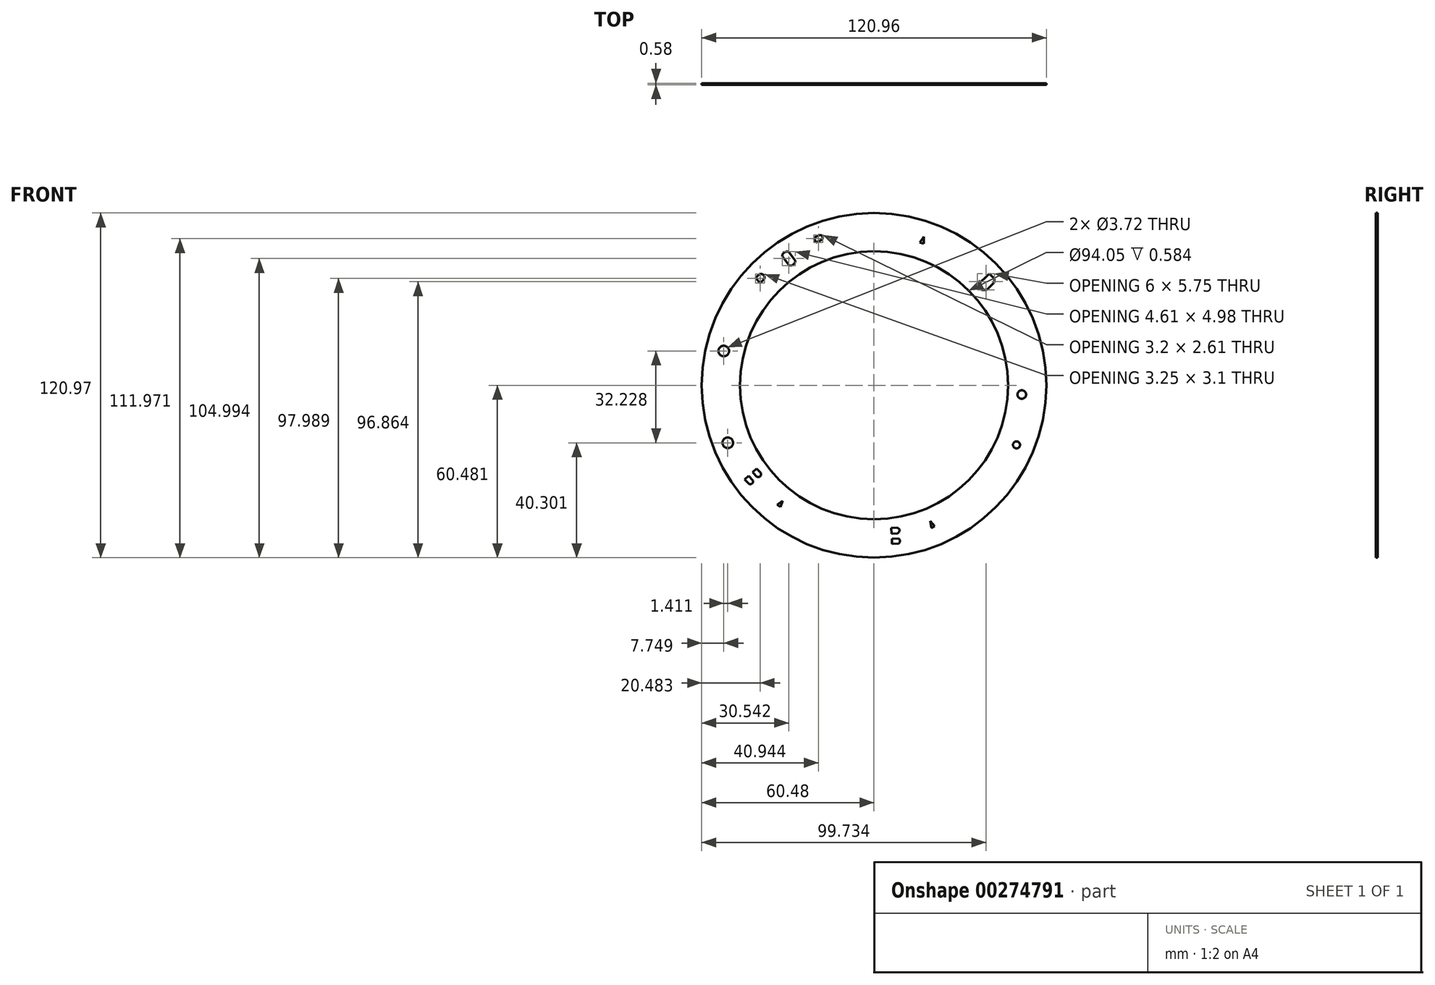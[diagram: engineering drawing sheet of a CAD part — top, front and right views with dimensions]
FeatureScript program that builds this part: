
annotation { "Feature Type Name" : "Feature", "Feature Type Description" : "" }
export const myFeature = defineFeature(function(context is Context, id is Id, definition is map)
    precondition{}
    {
        {
            var Q0;
            Q0=qCreatedBy(makeId("Front.planeOp"),FACE);
            var sketch = newSketch(context, id + "F0", { "sketchPlane" : qUnion([Q0])});
            skLineSegment(sketch, "E0", {"start": v(-42.5, 39.1) * mm, "end": v(-41.07, 40.5) * mm});
            skLineSegment(sketch, "E1", {"start": v(-41.07, 40.5) * mm, "end": v(-40, 40.5) * mm});
            skLineSegment(sketch, "E2", {"start": v(-40, 40.5) * mm, "end": v(-39.24, 39.72) * mm});
            skLineSegment(sketch, "E3", {"start": v(-39.24, 39.72) * mm, "end": v(-39.24, 38.92) * mm});
            skLineSegment(sketch, "E4", {"start": v(-42.5, 39.1) * mm, "end": v(-40.82, 37.39) * mm});
            skLineSegment(sketch, "E5", {"start": v(-39.24, 38.92) * mm, "end": v(-40.82, 37.39) * mm});
            skLineSegment(sketch, "E6", {"start": v(-32.93, 47.57) * mm, "end": v(-31.8, 48.43) * mm});
            skLineSegment(sketch, "E7", {"start": v(-30.94, 48.38) * mm, "end": v(-28.5, 45.16) * mm});
            skLineSegment(sketch, "E8", {"start": v(-28.68, 44.31) * mm, "end": v(-29.81, 43.45) * mm});
            skLineSegment(sketch, "E9", {"start": v(-30.67, 43.52) * mm, "end": v(-33.11, 46.74) * mm});
            skPoint(sketch, "E10.endSnap0", {"position": v(-17.59, 47.98) * mm});
            skPoint(sketch, "E11.orphan", {"position": v(-19.8, 47.65) * mm});
            skLineSegment(sketch, "E12", {"start": v(-22, 53.24) * mm, "end": v(-19.88, 54.23) * mm});
            skLineSegment(sketch, "E13", {"start": v(-19.08, 53.96) * mm, "end": v(-18.8, 53.38) * mm});
            skLineSegment(sketch, "E14", {"start": v(-19.12, 52.6) * mm, "end": v(-21.25, 51.61) * mm});
            skPoint(sketch, "E15.trimOffspring.end.orphan", {"position": v(-23.47, 56.4) * mm});
            skPoint(sketch, "E16.orphan", {"position": v(-15.17, 56.42) * mm});
            skLineSegment(sketch, "E17", {"start": v(-21.25, 51.61) * mm, "end": v(-22, 53.24) * mm});
            skLineSegment(sketch, "E18", {"start": v(-19.88, 54.23) * mm, "end": v(-19.08, 53.96) * mm});
            skLineSegment(sketch, "E19", {"start": v(-19.12, 52.6) * mm, "end": v(-18.8, 53.38) * mm});
            skPoint(sketch, "E20.orphan", {"position": v(-18.56, 51.4) * mm});
            skPoint(sketch, "E21.orphan", {"position": v(-19.32, 54.49) * mm});
            skPoint(sketch, "E22.orphan", {"position": v(-18.56, 52.86) * mm});
            skLineSegment(sketch, "E23", {"start": v(-30.94, 48.38) * mm, "end": v(-31.8, 48.43) * mm});
            skPoint(sketch, "E24.trimOffspring.end.orphan", {"position": v(-30.3, 46.4) * mm});
            skPoint(sketch, "E25.orphan", {"position": v(-30.18, 48.33) * mm});
            skLineSegment(sketch, "E26", {"start": v(-33.11, 46.74) * mm, "end": v(-32.93, 47.57) * mm});
            skLineSegment(sketch, "E27", {"start": v(-29.81, 43.45) * mm, "end": v(-30.67, 43.52) * mm});
            skLineSegment(sketch, "E28", {"start": v(-28.68, 44.31) * mm, "end": v(-28.5, 45.16) * mm});
            skPoint(sketch, "E29.endSnap0", {"position": v(15.6, 50.22) * mm});
            skLineSegment(sketch, "E30", {"start": v(15.2, 51.55) * mm, "end": v(16.54, 51.2) * mm});
            skLineSegment(sketch, "E31", {"start": v(16.54, 51.2) * mm, "end": v(16.54, 53.57) * mm});
            skLineSegment(sketch, "E32", {"start": v(16.54, 53.57) * mm, "end": v(15.2, 51.55) * mm});
            skLineSegment(sketch, "E33", {"start": v(39.6, 40.69) * mm, "end": v(41.38, 38.87) * mm});
            skLineSegment(sketch, "E34", {"start": v(41.38, 38.87) * mm, "end": v(41.38, 37.64) * mm});
            skLineSegment(sketch, "E35", {"start": v(41.38, 37.64) * mm, "end": v(38.63, 34.94) * mm});
            skLineSegment(sketch, "E36", {"start": v(38.63, 34.94) * mm, "end": v(36.97, 34.94) * mm});
            skLineSegment(sketch, "E37", {"start": v(39.6, 40.69) * mm, "end": v(35.39, 36.56) * mm});
            skPoint(sketch, "E38.orphan", {"position": v(44.33, 35.86) * mm});
            skLineSegment(sketch, "E39", {"start": v(35.39, 36.56) * mm, "end": v(36.97, 34.94) * mm});
            skLineSegment(sketch, "E40", {"start": v(-46.23, -31.56) * mm, "end": v(-44.67, -33.27) * mm});
            skLineSegment(sketch, "E41", {"start": v(-44.67, -33.27) * mm, "end": v(-43.98, -33.3) * mm});
            skLineSegment(sketch, "E42", {"start": v(-43.98, -33.3) * mm, "end": v(-43.4, -32.78) * mm});
            skLineSegment(sketch, "E43", {"start": v(-43.4, -32.78) * mm, "end": v(-43.35, -32.02) * mm});
            skLineSegment(sketch, "E44", {"start": v(-43.35, -32.02) * mm, "end": v(-44.89, -30.34) * mm});
            skLineSegment(sketch, "E45", {"start": v(-44.89, -30.34) * mm, "end": v(-46.23, -31.56) * mm});
            skLineSegment(sketch, "E46", {"start": v(-42.07, -27.76) * mm, "end": v(-40.57, -29.4) * mm});
            skLineSegment(sketch, "E47", {"start": v(-43.51, -29.08) * mm, "end": v(-42.07, -27.76) * mm});
            skLineSegment(sketch, "E48", {"start": v(-41.06, -30.71) * mm, "end": v(-40.57, -30.27) * mm});
            skLineSegment(sketch, "E49", {"start": v(-40.57, -30.27) * mm, "end": v(-40.57, -29.4) * mm});
            skLineSegment(sketch, "E50", {"start": v(-43.51, -29.08) * mm, "end": v(-42.02, -30.71) * mm});
            skLineSegment(sketch, "E51", {"start": v(-42.02, -30.71) * mm, "end": v(-41.06, -30.71) * mm});
            skLineSegment(sketch, "E52", {"start": v(-34.82, -40.57) * mm, "end": v(-33.66, -41.33) * mm});
            skLineSegment(sketch, "E53", {"start": v(-33.66, -41.33) * mm, "end": v(-32.93, -39.06) * mm});
            skLineSegment(sketch, "E54", {"start": v(-32.93, -39.06) * mm, "end": v(-34.82, -40.57) * mm});
            skLineSegment(sketch, "E55", {"start": v(19.2, -48.67) * mm, "end": v(20.44, -48.04) * mm});
            skLineSegment(sketch, "E56", {"start": v(20.44, -48.04) * mm, "end": v(18.84, -46.28) * mm});
            skLineSegment(sketch, "E57", {"start": v(18.84, -46.28) * mm, "end": v(19.2, -48.67) * mm});
            skLineSegment(sketch, "E58", {"start": v(5.46, -54.28) * mm, "end": v(7.76, -54.16) * mm});
            skLineSegment(sketch, "E59", {"start": v(7.76, -54.16) * mm, "end": v(8.24, -53.65) * mm});
            skLineSegment(sketch, "E60", {"start": v(8.24, -53.65) * mm, "end": v(8.2, -52.87) * mm});
            skLineSegment(sketch, "E61", {"start": v(8.2, -52.87) * mm, "end": v(7.64, -52.35) * mm});
            skLineSegment(sketch, "E62", {"start": v(7.64, -52.35) * mm, "end": v(5.36, -52.48) * mm});
            skLineSegment(sketch, "E63", {"start": v(5.36, -52.48) * mm, "end": v(5.46, -54.28) * mm});
            skLineSegment(sketch, "E64", {"start": v(5.15, -48.66) * mm, "end": v(7.37, -48.54) * mm});
            skLineSegment(sketch, "E65", {"start": v(5.26, -50.61) * mm, "end": v(5.15, -48.66) * mm});
            skLineSegment(sketch, "E66", {"start": v(8.07, -49.75) * mm, "end": v(8.04, -49.1) * mm});
            skLineSegment(sketch, "E67", {"start": v(8.04, -49.1) * mm, "end": v(7.37, -48.54) * mm});
            skLineSegment(sketch, "E68", {"start": v(5.26, -50.61) * mm, "end": v(7.46, -50.5) * mm});
            skLineSegment(sketch, "E69", {"start": v(7.46, -50.5) * mm, "end": v(8.07, -49.75) * mm});
            skCircle(sketch, "E70", {"center": v(-52.19, -18.75) * mm, "radius": 1.86 * mm});
            skCircle(sketch, "E71", {"center": v(-53.6, 13.48) * mm, "radius": 1.86 * mm});
            skCircle(sketch, "E72", {"center": v(49.12, -19.48) * mm, "radius": 1.23 * mm});
            skCircle(sketch, "E73", {"center": v(50.98, -1.8) * mm, "radius": 1.5 * mm});
            skCircle(sketch, "E74", {"center": v(-0.87, 1.43) * mm, "radius": 47.02 * mm});
            skCircle(sketch, "E75", {"center": v(-0.87, 1.43) * mm, "radius": 60.48 * mm});
            skSolve(sketch);
        }
        {
            var Q0;
            Q0=makeQuery(id+"F0.imprint","IMPRINT",FACE,{"disambiguationData":[TD([[makeQuery(id+"F0.imprint","IMPRINT",EDGE,{"derivedFrom":sQuery(id+"F0.wireOp",EDGE,"E0")}),1.0]])]});
            extrude(context, id + "F1", {"entities" : qUnion([Q0]), "depth" : 0.58 * mm});
        }
    });
